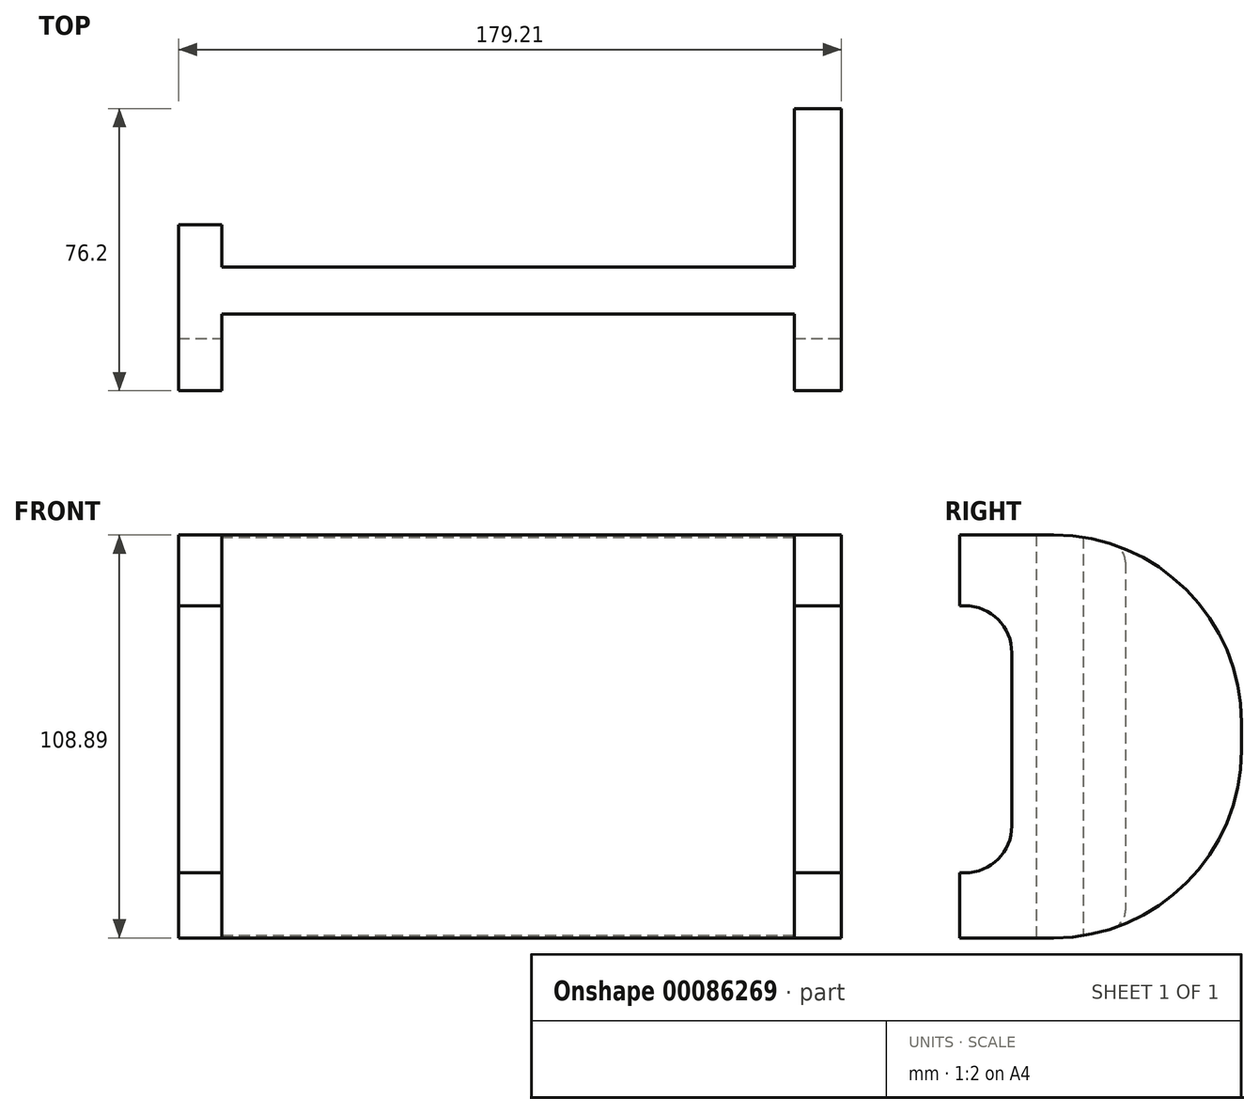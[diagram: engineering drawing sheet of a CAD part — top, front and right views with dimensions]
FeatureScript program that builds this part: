
annotation { "Feature Type Name" : "Feature", "Feature Type Description" : "" }
export const myFeature = defineFeature(function(context is Context, id is Id, definition is map)
    precondition{}
    {
        {
            var Q0;
            Q0=qCreatedBy(makeId("Top.planeOp"),FACE);
            var sketch = newSketch(context, id + "F0", { "sketchPlane" : qUnion([Q0])});
            skLineSegment(sketch, "E0.bottom", {"start": v(-78.58, 19.3) * mm, "end": v(76.26, 19.3) * mm});
            skLineSegment(sketch, "E0.top", {"start": v(-78.58, 6.6) * mm, "end": v(76.26, 6.6) * mm});
            skLineSegment(sketch, "E1.bottom", {"start": v(76.26, 62.1) * mm, "end": v(88.96, 62.1) * mm});
            skLineSegment(sketch, "E1.top", {"start": v(76.26, -14.1) * mm, "end": v(88.96, -14.1) * mm});
            skLineSegment(sketch, "E1.left", {"start": v(76.26, 62.1) * mm, "end": v(76.26, 19.3) * mm});
            skLineSegment(sketch, "E1.right", {"start": v(88.96, 62.1) * mm, "end": v(88.96, -14.1) * mm});
            skLineSegment(sketch, "E2.bottom", {"start": v(-78.58, 30.73) * mm, "end": v(-90.25, 30.73) * mm});
            skLineSegment(sketch, "E2.top", {"start": v(-78.58, -14.1) * mm, "end": v(-90.25, -14.1) * mm});
            skLineSegment(sketch, "E2.left", {"start": v(-78.58, 30.73) * mm, "end": v(-78.58, 19.3) * mm});
            skLineSegment(sketch, "E2.right", {"start": v(-90.25, 30.73) * mm, "end": v(-90.25, -14.1) * mm});
            skLineSegment(sketch, "E3.trimOffspring", {"start": v(76.26, 6.6) * mm, "end": v(76.26, -14.1) * mm});
            skLineSegment(sketch, "E4.trimOffspring", {"start": v(-78.58, 6.6) * mm, "end": v(-78.58, -14.1) * mm});
            skSolve(sketch);
        }
        {
            var Q0;
            Q0=makeQuery(id+"F0.imprint","IMPRINT",FACE,{"disambiguationData":[TD([[makeQuery(id+"F0.imprint","IMPRINT",EDGE,{"derivedFrom":sQuery(id+"F0.wireOp",EDGE,"E0.bottom")}),-1.0]])]});
            extrude(context, id + "F1", {"entities" : qUnion([Q0]), "depth" : 108.89 * mm});
        }
        {
            var Q0;
            Q0=makeQuery(id+"F1.opExtrude","CAP_EDGE",EDGE,{"disambiguationData":[OSD([sQuery(id+"F0.wireOp",EDGE,"E1.bottom")])],"isStart":false});
            var Q1;
            Q1=makeQuery(id+"F1.opExtrude","CAP_EDGE",EDGE,{"disambiguationData":[OSD([sQuery(id+"F0.wireOp",EDGE,"E1.bottom")])],"isStart":true});
            fillet(context, id + "F2", {"entities" : qUnion([Q0, Q1]), "radius" : 50.8 * mm, "tangentPropagation" : true, "allowEdgeOverflow" : false});
        }
        {
            var Q0;
            Q0=makeQuery(id+"F2.opFillet","BLEND_EDGE",EDGE,{"blendedFrom":[makeQuery(id+"F1.opExtrude","CAP_EDGE",EDGE,{"disambiguationData":[OSD([sQuery(id+"F0.wireOp",EDGE,"E1.bottom")])],"isStart":false}),makeQuery(id+"F1.opExtrude","SWEPT_FACE",FACE,{"disambiguationData":[OSD([sQuery(id+"F0.wireOp",EDGE,"E2.bottom")])]})],"blendedInto":[makeQuery(id+"F1.opExtrude","SWEPT_FACE",FACE,{"disambiguationData":[OSD([sQuery(id+"F0.wireOp",EDGE,"E2.bottom")])]})]});
            var Q1;
            Q1=makeQuery(id+"F2.opFillet","BLEND_EDGE",EDGE,{"blendedFrom":[makeQuery(id+"F1.opExtrude","CAP_EDGE",EDGE,{"disambiguationData":[OSD([sQuery(id+"F0.wireOp",EDGE,"E1.bottom")])],"isStart":true}),makeQuery(id+"F1.opExtrude","SWEPT_FACE",FACE,{"disambiguationData":[OSD([sQuery(id+"F0.wireOp",EDGE,"E2.bottom")])]})],"blendedInto":[makeQuery(id+"F1.opExtrude","SWEPT_FACE",FACE,{"disambiguationData":[OSD([sQuery(id+"F0.wireOp",EDGE,"E2.bottom")])]})]});
            fillet(context, id + "F3", {"entities" : qUnion([Q0, Q1]), "radius" : 5.08 * mm, "tangentPropagation" : true, "allowEdgeOverflow" : false});
        }
        {
            var Q0;
            Q0=qCreatedBy(makeId("Right.planeOp"),FACE);
            var sketch = newSketch(context, id + "F4", { "sketchPlane" : qUnion([Q0])});
            skLineSegment(sketch, "E5.bottom", {"start": v(-12.7, 89.76) * mm, "end": v(-24.03, 89.76) * mm});
            skLineSegment(sketch, "E5.top", {"start": v(-12.7, 17.56) * mm, "end": v(-24.03, 17.56) * mm});
            skLineSegment(sketch, "E5.left", {"start": v(0, 77.06) * mm, "end": v(0, 30.26) * mm});
            skLineSegment(sketch, "E5.right", {"start": v(-24.03, 89.76) * mm, "end": v(-24.03, 17.56) * mm});
            skPoint(sketch, "E6.visualSharp", {"position": v(0, 89.76) * mm});
            skArc(sketch, "E6.filletArc", {"start": v(0, 77.06) * mm, "mid": v(-3.72, 86.04) * mm, "end": v(-12.7, 89.76) * mm});
            skPoint(sketch, "E7.visualSharp", {"position": v(0, 17.56) * mm});
            skArc(sketch, "E7.filletArc", {"start": v(-12.7, 17.56) * mm, "mid": v(-3.72, 21.28) * mm, "end": v(0, 30.26) * mm});
            skSolve(sketch);
        }
        {
            var Q0;
            Q0=makeQuery(id+"F4.imprint","IMPRINT",FACE,{"disambiguationData":[TD([[makeQuery(id+"F4.imprint","IMPRINT",EDGE,{"derivedFrom":sQuery(id+"F4.wireOp",EDGE,"E5.bottom")}),1.0]])]});
            extrude(context, id + "F5", {"entities" : qUnion([Q0]), "operationType" : NewBodyOperationType.REMOVE, "endBound" : BoundingType.SYMMETRIC, "oppositeDirection" : true, "depth" : 1270 * mm});
        }
    });
